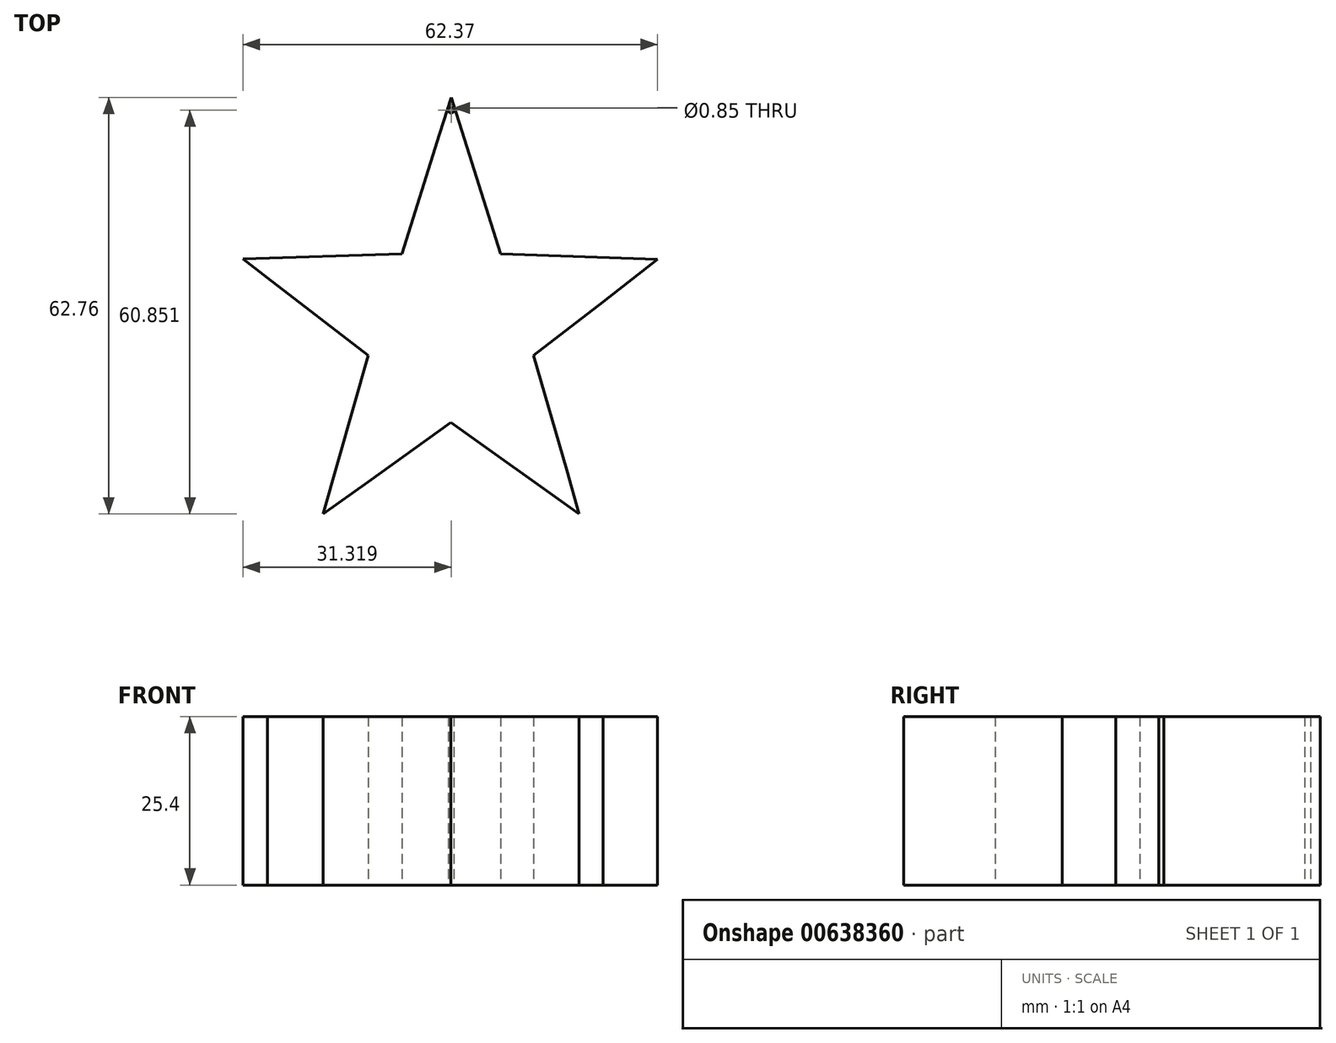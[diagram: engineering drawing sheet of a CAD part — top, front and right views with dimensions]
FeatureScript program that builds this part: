
annotation { "Feature Type Name" : "Feature", "Feature Type Description" : "" }
export const myFeature = defineFeature(function(context is Context, id is Id, definition is map)
    precondition{}
    {
        {
            var Q0;
            Q0=qCreatedBy(makeId("Top.planeOp"),FACE);
            var sketch = newSketch(context, id + "F0", { "sketchPlane" : qUnion([Q0])});
            skLineSegment(sketch, "E0", {"start": v(-30.35, 46.83) * mm, "end": v(-35.4, 62.96) * mm});
            skLineSegment(sketch, "E1", {"start": v(-35.4, 62.96) * mm, "end": v(-37.78, 70.38) * mm});
            skLineSegment(sketch, "E2", {"start": v(-37.78, 70.38) * mm, "end": v(-39.52, 64.88) * mm});
            skLineSegment(sketch, "E3", {"start": v(-39.52, 64.88) * mm, "end": v(-45.21, 46.79) * mm});
            skLineSegment(sketch, "E4", {"start": v(-45.21, 46.79) * mm, "end": v(-69.1, 46.06) * mm});
            skLineSegment(sketch, "E5", {"start": v(-69.1, 46.06) * mm, "end": v(-65.43, 43.17) * mm});
            skLineSegment(sketch, "E6", {"start": v(-65.43, 43.17) * mm, "end": v(-50.28, 31.49) * mm});
            skLineSegment(sketch, "E7", {"start": v(-50.28, 31.49) * mm, "end": v(-57.06, 7.62) * mm});
            skLineSegment(sketch, "E8", {"start": v(-57.06, 7.62) * mm, "end": v(-50.28, 12.5) * mm});
            skLineSegment(sketch, "E9", {"start": v(-50.28, 12.5) * mm, "end": v(-37.8, 21.42) * mm});
            skLineSegment(sketch, "E10", {"start": v(-37.8, 21.42) * mm, "end": v(-18.5, 7.62) * mm});
            skLineSegment(sketch, "E11", {"start": v(-18.5, 7.62) * mm, "end": v(-20.38, 14.23) * mm});
            skLineSegment(sketch, "E12", {"start": v(-20.38, 14.23) * mm, "end": v(-25.35, 31.49) * mm});
            skLineSegment(sketch, "E13", {"start": v(-25.35, 31.49) * mm, "end": v(-14.88, 39.57) * mm});
            skLineSegment(sketch, "E14", {"start": v(-14.88, 39.57) * mm, "end": v(-7.84, 45.15) * mm});
            skLineSegment(sketch, "E15", {"start": v(-7.84, 45.15) * mm, "end": v(-6.73, 46.02) * mm});
            skLineSegment(sketch, "E16", {"start": v(-6.73, 46.02) * mm, "end": v(-30.35, 46.83) * mm});
            skCircle(sketch, "E17", {"center": v(-37.78, 68.47) * mm, "radius": 0.43 * mm});
            skSolve(sketch);
        }
        {
            var Q0;
            Q0 = qSketchRegion(id + "F0", true);
            extrude(context, id + "F1", {"entities" : qUnion([Q0]), "depth" : 25.4 * mm, "offsetDistance" : 25.4 * mm});
        }
    });
